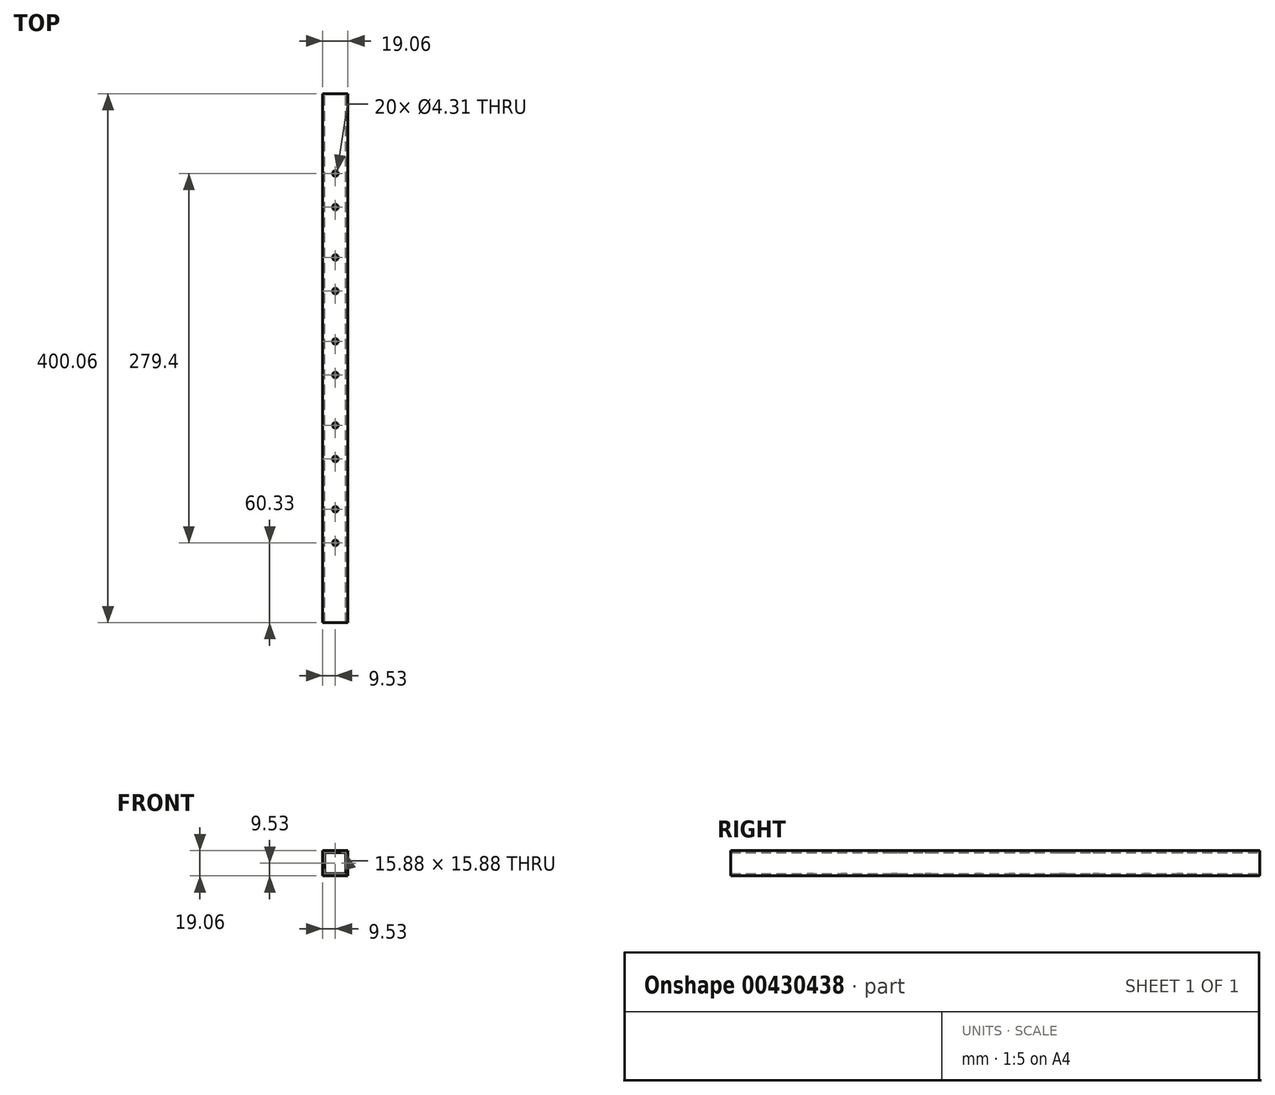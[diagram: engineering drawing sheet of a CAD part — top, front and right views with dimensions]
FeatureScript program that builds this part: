
annotation { "Feature Type Name" : "Feature", "Feature Type Description" : "" }
export const myFeature = defineFeature(function(context is Context, id is Id, definition is map)
    precondition{}
    {
        {
            var Q0;
            Q0=qCreatedBy(makeId("Front.planeOp"),FACE);
            var sketch = newSketch(context, id + "F0", { "sketchPlane" : qUnion([Q0])});
            skLineSegment(sketch, "E0.bottom", {"start": v(-9.52, 9.53) * mm, "end": v(9.53, 9.53) * mm});
            skLineSegment(sketch, "E0.top", {"start": v(-9.53, -9.53) * mm, "end": v(9.52, -9.53) * mm});
            skLineSegment(sketch, "E0.left", {"start": v(-9.52, 9.53) * mm, "end": v(-9.53, -9.52) * mm});
            skLineSegment(sketch, "E0.right", {"start": v(9.53, 9.53) * mm, "end": v(9.52, -9.52) * mm});
            skPoint(sketch, "E0.middle", {"position": v(0, 0) * mm});
            skLineSegment(sketch, "E1.bottom", {"start": v(-7.94, 7.94) * mm, "end": v(7.94, 7.94) * mm});
            skLineSegment(sketch, "E1.top", {"start": v(-7.94, -7.94) * mm, "end": v(7.94, -7.94) * mm});
            skLineSegment(sketch, "E1.left", {"start": v(-7.94, 7.94) * mm, "end": v(-7.94, -7.94) * mm});
            skLineSegment(sketch, "E1.right", {"start": v(7.94, 7.94) * mm, "end": v(7.94, -7.94) * mm});
            skSolve(sketch);
        }
        {
            var Q0;
            Q0 = qSketchRegion(id + "F0", true);
            extrude(context, id + "F1", {"entities" : qUnion([Q0]), "depth" : 400.05 * mm, "offsetDistance" : 25.4 * mm, "symmetric" : true});
        }
        {
            var Q0;
            Q0=makeQuery(id+"F1.opExtrude","SWEPT_FACE",FACE,{"disambiguationData":[OSD([sQuery(id+"F0.wireOp",EDGE,"E0.bottom")])]});
            var sketch = newSketch(context, id + "F2", { "sketchPlane" : qUnion([Q0])});
            skCircle(sketch, "E2", {"center": v(0, 12.7) * mm, "radius": 2.15 * mm});
            skCircle(sketch, "E3.MirrorC", {"center": v(0, -12.7) * mm, "radius": 2.15 * mm});
            skCircle(sketch, "E4.0.1.0", {"center": v(0, 76.2) * mm, "radius": 2.15 * mm});
            skCircle(sketch, "E4.0.1.1", {"center": v(0, 50.8) * mm, "radius": 2.15 * mm});
            skCircle(sketch, "E4.0.2.0", {"center": v(0, 139.7) * mm, "radius": 2.15 * mm});
            skCircle(sketch, "E4.0.2.1", {"center": v(0, 114.3) * mm, "radius": 2.15 * mm});
            skLineSegment(sketch, "E4.direction1", {"start": v(0, 12.7) * mm, "end": v(25.4, 12.7) * mm, "construction": true});
            skLineSegment(sketch, "E4.direction2", {"start": v(0, 12.7) * mm, "end": v(0, 76.2) * mm, "construction": true});
            skCircle(sketch, "E5.MirrorC", {"center": v(0, -50.8) * mm, "radius": 2.15 * mm});
            skCircle(sketch, "E6.MirrorC", {"center": v(0, -76.2) * mm, "radius": 2.15 * mm});
            skCircle(sketch, "E7.MirrorC", {"center": v(0, -114.3) * mm, "radius": 2.15 * mm});
            skCircle(sketch, "E8.MirrorC", {"center": v(0, -139.7) * mm, "radius": 2.15 * mm});
            skSolve(sketch);
        }
        {
            var Q0;
            Q0 = qSketchRegion(id + "F2", true);
            var Q1;
            Q1=makeQuery(id+"F1.opExtrude","SWEPT_FACE",FACE,{"disambiguationData":[OSD([sQuery(id+"F0.wireOp",EDGE,"E0.top")])]});
            extrude(context, id + "F3", {"entities" : qUnion([Q0, Q1]), "operationType" : NewBodyOperationType.REMOVE, "oppositeDirection" : true, "depth" : 25.4 * mm});
        }
    });
